# Revit family: Power-ModularDevices-GEWISS-90AM-ENERGY_METER_DIGITAL_SINGLE_PHASE
name_source: partatom
category: Apparecchi elettrici
revit_build: Autodesk Revit 2016 (Build: 20161004_0715(x64)
units: mm (PartAtom-declared; Revit-internal decimal feet)

## family parameters
Condiviso = No
Host = Superficie
Mantenere orientamento annotazione = Sì
Numero OmniClass = 23.80.30.00
Punto di calcolo locali = Sì
Quota connettore circolare = Usa diametro
Taglio con vuoti quando caricato = No
Tipo di parte = Normale
Titolo OmniClass = Distribution Devices

## types (2) — shared parameters
A = 18 mm  [stored 0.0590551 ft]
Accuracy rate = 1
B = 85 mm  [stored 0.278871 ft]
C = 59 mm
Catalogue = POWER
Catalogue Range = 90 AM
D = 45 mm  [stored 0.147638 ft]
Electrocod = 163
Fin_Amperometro = <Per categoria>
I max (A) = 32A
IDF = 50499170-d10d-4bbd-b870-ca51359950bc
IDT = 520d1e2c-82c1-49bd-bafd-3cb3aeb46d35
IP degree = IP20
Immagine tipo = GWD6801.jpg
Installation = DIN rail
No. Chorus modules = 1
Numero poli = 1
Potenza in Watt = 0 V
Produttore = GEWISS S.p.A.
Prospetto di default = 1219 mm
Rated voltage = 230Vac
Supply voltage = 230Vac - 50Hz
Technical sheet = https://www.gewiss.com
Type = Digital single-phase
URL = https://www.gewiss.com
Version file RFA = 18.0

## per-type parameters (varying)
| type | Descrizione | EAN code | Modello |
| GWD6801 - SINGLE PHASE ENERGY METER DIRECT 32A 1M | SINGLE PHASE ENERGY METER DIRECT 32A 1M | 8011564812413 | GWD6801 |
| GWD6802 - MID SINGLE PHASE METER DIRECT 32A 1M | MID SINGLE PHASE METER DIRECT 32A 1M | 8011564886759 | GWD6802 |

note: [stored X ft] marks values corroborated as IEEE doubles in the binary element streams (Revit-internal decimal feet)
